# Revit family: 819010001_Asiento Institucional Solid
name_source: partatom
category: Plumbing Fixtures
units: mm (PartAtom-declared; Revit-internal decimal feet)

## family parameters
Always vertical = Yes
Cut with Voids When Loaded = No
OmniClass Number = 23.31.15.13
OmniClass Title = Sitz Baths
Part Type = Normal
Room Calculation Point = No
Round Connector Dimension = Use Diameter
Shared = No
Work Plane-Based = No

## types (1)
- 819010001_Asiento Institucional Solid
    Ancho = 360 mm  [stored 1.1811 ft]
    Componentes de instalación = · Tuercas en Polipropileno (PP) x 2 unds.
· Seegers en acero inoxidable x 2 unds.
· Pasador en aluminio x 2 unds.
· Antideslizantes en Policloruro de Vinilo (PVC) x 2 unds.
    Creado por = BIMBAU
    Cuidado Y Limpieza = -Haga limpieza únicamente con jabones suaves o de tocador. -No utilice jabones o desinfectantes fuertes, como cloro o ácido muriático. -Utilice siempre para su limpieza un paño suave. -Evite la exposición a la luz solar directa, para prevenir pérdidas en la coloración del asiento.
    Default Elevation = 0 mm  [stored 0 ft]
    Description = -Alto tráfico. -Anti-bacterial. -Herrajes plásticos reforzados. -Fácil instalación, limpieza y mantenimiento. -Inyectado en polímero de alta resistencia y durabilidad.
    Fecha de creación = 13/04/2021
    Manufacturer = Corona
    Material = Corona_Polimero
    Model = Asiento Institucional Solid
    Profundidad = 457 mm  [stored 1.49934 ft]
    Referencia = 819010001
    Resistencia a la flexión = 1335 ± 22 N - 300 ± 5 lbs.
    URL = https://corona.co

note: [stored X ft] marks values corroborated as IEEE doubles in the binary element streams (Revit-internal decimal feet)

## geometry (parser evidence)
native form markers: Sweep x2
no freeform markers — native parametric forms only
